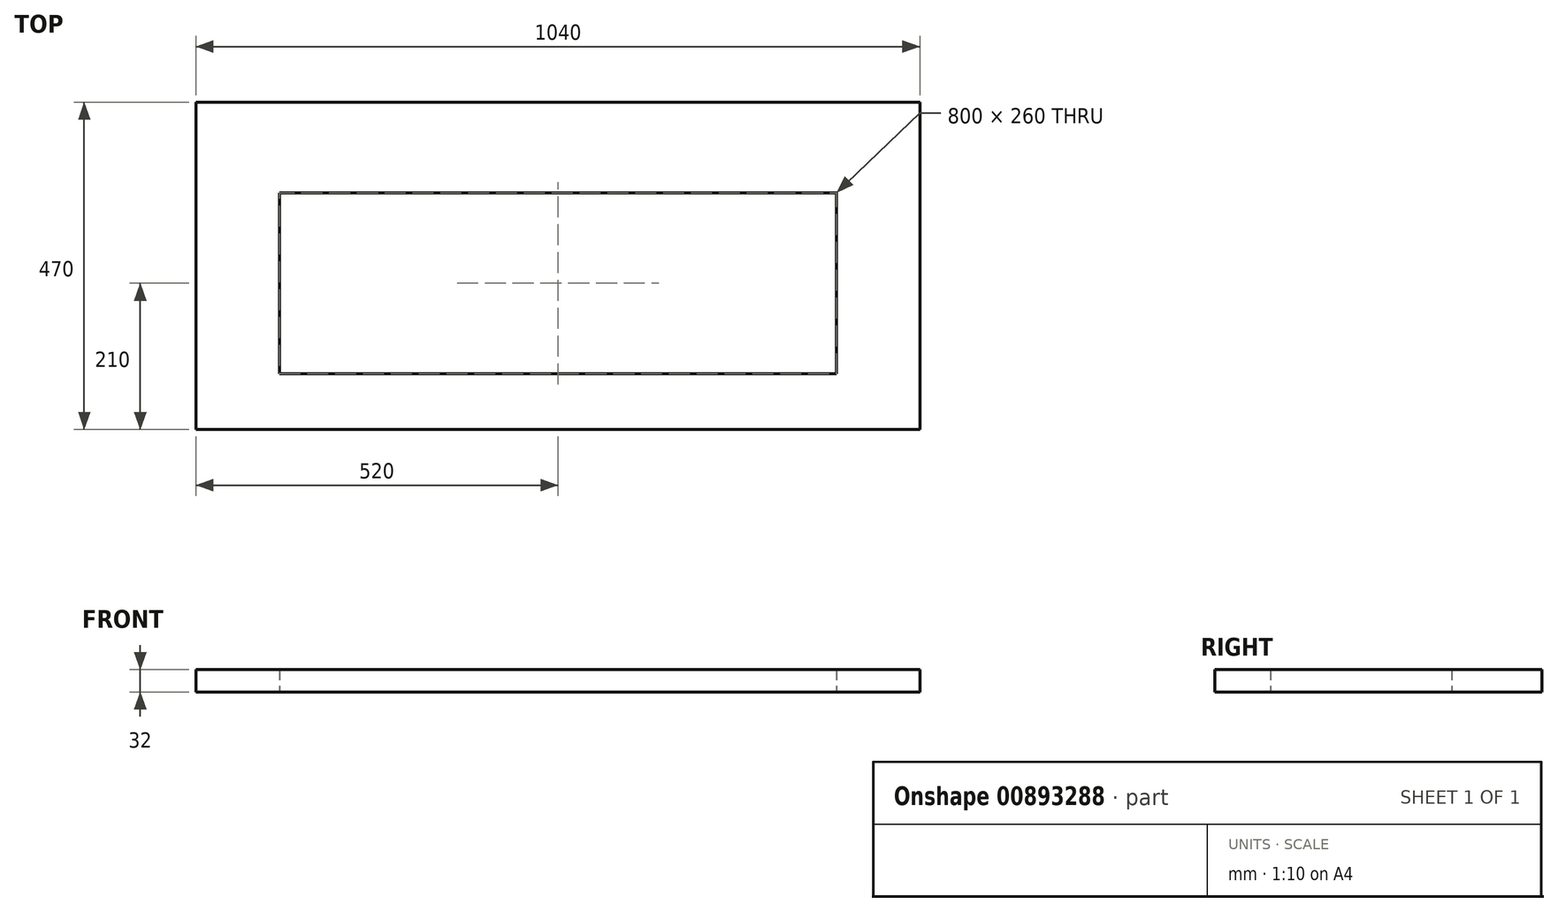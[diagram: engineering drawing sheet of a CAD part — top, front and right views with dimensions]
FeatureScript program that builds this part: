
annotation { "Feature Type Name" : "Feature", "Feature Type Description" : "" }
export const myFeature = defineFeature(function(context is Context, id is Id, definition is map)
    precondition{}
    {
        {
            var Q0;
            Q0=qCreatedBy(makeId("Top.planeOp"),FACE);
            var sketch = newSketch(context, id + "F0", { "sketchPlane" : qUnion([Q0])});
            skLineSegment(sketch, "E0.bottom", {"start": v(520, 235) * mm, "end": v(-520, 235) * mm});
            skLineSegment(sketch, "E0.top", {"start": v(520, -235) * mm, "end": v(-520, -235) * mm});
            skLineSegment(sketch, "E0.left", {"start": v(520, 235) * mm, "end": v(520, -235) * mm});
            skLineSegment(sketch, "E0.right", {"start": v(-520, 235) * mm, "end": v(-520, -235) * mm});
            skPoint(sketch, "E0.middle", {"position": v(0, 0) * mm});
            skSolve(sketch);
        }
        {
            var Q0;
            Q0=makeQuery(id+"F0.imprint","IMPRINT",FACE,{"disambiguationData":[TD([[makeQuery(id+"F0.imprint","IMPRINT",EDGE,{"derivedFrom":sQuery(id+"F0.wireOp",EDGE,"E0.bottom")}),1.0]])]});
            extrude(context, id + "F1", {"entities" : qUnion([Q0]), "depth" : 32 * mm, "offsetDistance" : 25 * mm});
        }
        {
            var Q0;
            Q0=qCreatedBy(makeId("Top.planeOp"),FACE);
            var sketch = newSketch(context, id + "F2", { "sketchPlane" : qUnion([Q0])});
            skLineSegment(sketch, "E1.bottom", {"start": v(400, 105) * mm, "end": v(-400, 105) * mm});
            skLineSegment(sketch, "E1.top", {"start": v(400, -155) * mm, "end": v(-400, -155) * mm});
            skLineSegment(sketch, "E1.left", {"start": v(400, 105) * mm, "end": v(400, -155) * mm});
            skLineSegment(sketch, "E1.right", {"start": v(-400, 105) * mm, "end": v(-400, -155) * mm});
            skPoint(sketch, "E1.middle", {"position": v(0, -25) * mm});
            skSolve(sketch);
        }
        {
            var Q0;
            Q0 = qSketchRegion(id + "F2", true);
            extrude(context, id + "F3", {"entities" : qUnion([Q0]), "operationType" : NewBodyOperationType.REMOVE, "endBound" : BoundingType.THROUGH_ALL, "depth" : 25 * mm, "offsetDistance" : 25 * mm});
        }
        {
            var Q0;
            Q0=qCreatedBy(makeId("Right.planeOp"),FACE);
            var sketch = newSketch(context, id + "F4", { "sketchPlane" : qUnion([Q0])});
            skCircle(sketch, "E2", {"center": v(-95, 16) * mm, "radius": 4 * mm});
            skCircle(sketch, "E3", {"center": v(45, 16) * mm, "radius": 4 * mm});
            skSolve(sketch);
        }
        {
            var Q0;
            Q0=makeQuery(id+"F3.boolean.opBoolean","COPY",FACE,{"derivedFrom":makeQuery(id+"F3.opExtrude","SWEPT_FACE",FACE,{"disambiguationData":[OSD([sQuery(id+"F2.wireOp",EDGE,"E1.right")])]})});
            var sketch = newSketch(context, id + "F5", { "sketchPlane" : qUnion([Q0])});
            skCircle(sketch, "E4", {"center": v(-95, 16) * mm, "radius": 8 * mm});
            skCircle(sketch, "E5", {"center": v(45, 16) * mm, "radius": 8 * mm});
            skSolve(sketch);
        }
        {
            var Q0;
            Q0=makeQuery(id+"F3.boolean.opBoolean","COPY",FACE,{"derivedFrom":makeQuery(id+"F3.opExtrude","SWEPT_FACE",FACE,{"disambiguationData":[OSD([sQuery(id+"F2.wireOp",EDGE,"E1.left")])]})});
            var sketch = newSketch(context, id + "F6", { "sketchPlane" : qUnion([Q0])});
            skCircle(sketch, "E6.0", {"center": v(-45, 16) * mm, "radius": 10 * mm});
            skCircle(sketch, "E7.0", {"center": v(95, 16) * mm, "radius": 10 * mm});
            skSolve(sketch);
        }
        {
            var Q0;
            Q0=makeQuery(id+"F1.opExtrude","CAP_FACE",FACE,{"disambiguationData":[OSD([sQuery(id+"F0.wireOp",EDGE,"E0.bottom"),sQuery(id+"F0.wireOp",EDGE,"E0.top"),sQuery(id+"F0.wireOp",EDGE,"E0.left"),sQuery(id+"F0.wireOp",EDGE,"E0.right")])],"isStart":false});
            var Q1;
            Q1=makeQuery(id+"F1.opExtrude","CAP_FACE",FACE,{"disambiguationData":[OSD([sQuery(id+"F0.wireOp",EDGE,"E0.bottom"),sQuery(id+"F0.wireOp",EDGE,"E0.top"),sQuery(id+"F0.wireOp",EDGE,"E0.left"),sQuery(id+"F0.wireOp",EDGE,"E0.right")])],"isStart":true});
            cPlane(context, id + "F7", {"entities" : qUnion([Q0, Q1]), "cplaneType" : CPlaneType.MID_PLANE, "offset" : 25 * mm, "width" : 150 * mm, "height" : 150 * mm});
        }
    });
